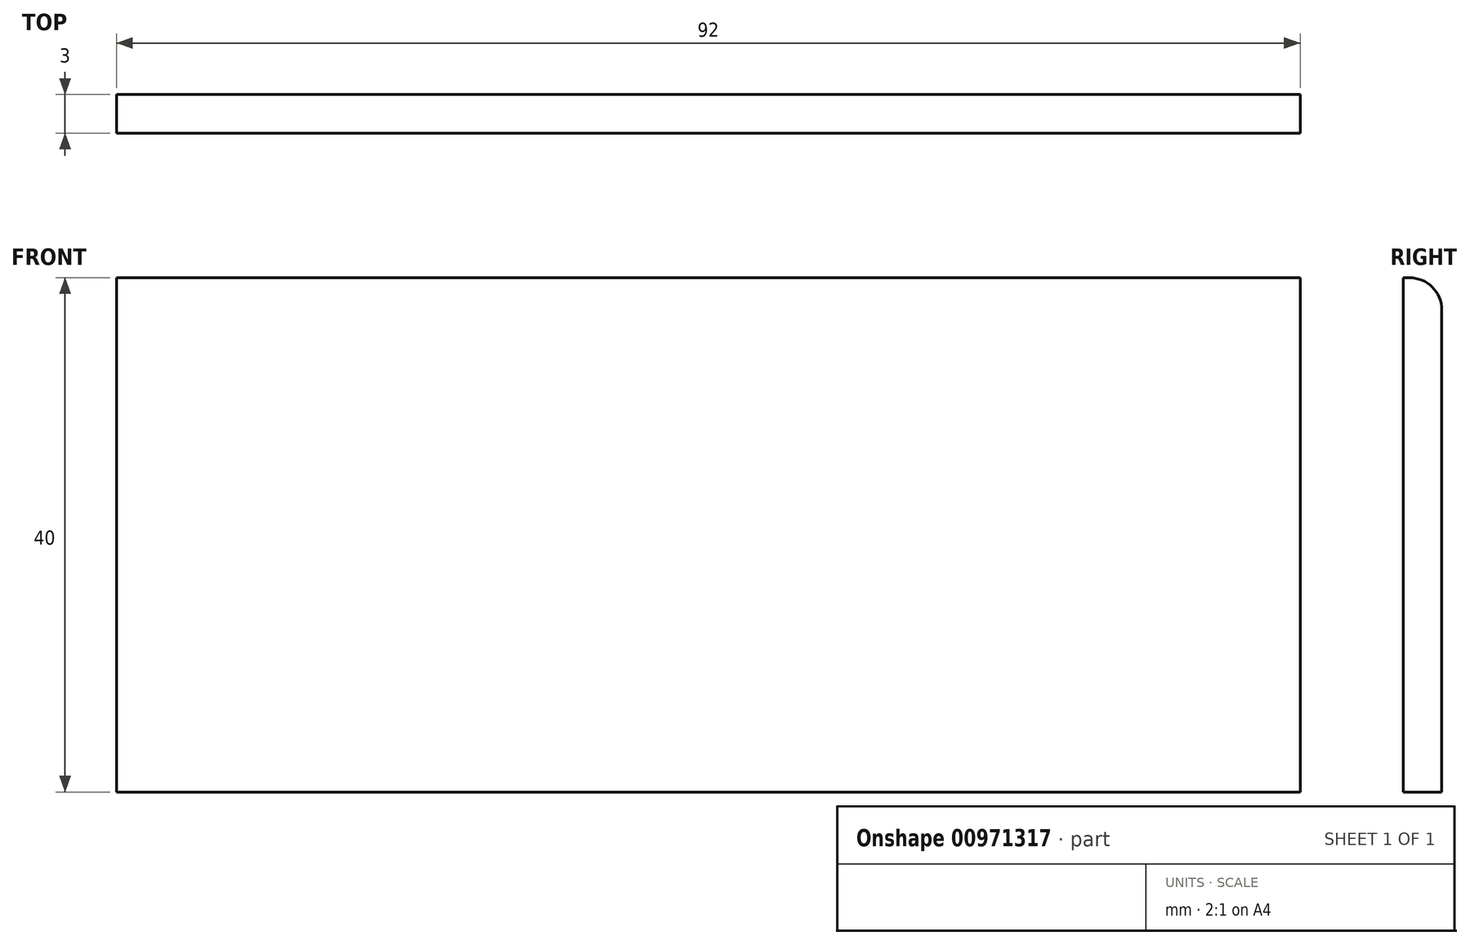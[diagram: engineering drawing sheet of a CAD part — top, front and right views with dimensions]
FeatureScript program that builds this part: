
annotation { "Feature Type Name" : "Feature", "Feature Type Description" : "" }
export const myFeature = defineFeature(function(context is Context, id is Id, definition is map)
    precondition{}
    {
        {
            var Q0;
            Q0=qCreatedBy(makeId("Top.planeOp"),FACE);
            var sketch = newSketch(context, id + "F0", { "sketchPlane" : qUnion([Q0])});
            skLineSegment(sketch, "E0.bottom", {"start": v(46, -1.5) * mm, "end": v(-46, -1.5) * mm});
            skLineSegment(sketch, "E0.top", {"start": v(46, 1.5) * mm, "end": v(-46, 1.5) * mm});
            skLineSegment(sketch, "E0.left", {"start": v(46, -1.5) * mm, "end": v(46, 1.5) * mm});
            skLineSegment(sketch, "E0.right", {"start": v(-46, -1.5) * mm, "end": v(-46, 1.5) * mm});
            skPoint(sketch, "E0.middle", {"position": v(0, 0) * mm});
            skSolve(sketch);
        }
        {
            var Q0;
            Q0 = qSketchRegion(id + "F0", true);
            extrude(context, id + "F1", {"entities" : qUnion([Q0]), "depth" : 40 * mm, "offsetDistance" : 25 * mm});
        }
        {
            var Q0;
            Q0=makeQuery(id+"F1.opExtrude","CAP_EDGE",EDGE,{"disambiguationData":[OSD([sQuery(id+"F0.wireOp",EDGE,"E0.top")])],"isStart":false});
            fillet(context, id + "F2", {"entities" : qUnion([Q0]), "radius" : 2.5 * mm, "tangentPropagation" : true, "allowEdgeOverflow" : false});
        }
    });
